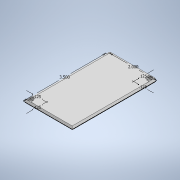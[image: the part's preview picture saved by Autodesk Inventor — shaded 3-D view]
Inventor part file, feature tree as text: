
AUTODESK INVENTOR PART (.ipt)
format: ipt  version: 2020 (Build 240168000, 168)  size: 122,880 bytes
history: native  units: in
note: dims shown in document units (in); Inventor stores cm internally (conversion verified against a paired STEP export)
features: sketch x2, extrude x1, hole x1, fillet x1
ambient origin geometry x8: Origin, YZ Plane, XZ Plane, XY Plane, X Axis, Y Axis, Z Axis, Center Point
bodies: Solid1 (feature_tree)
feature tree (5):
  sketch  "Sketch1"  dims[d0=2.0in d1=3.5in]
  extrude  "Extrusion1"  Depth=2.0in
  hole  "Hole2"  [1 undecoded]
  fillet  "Fillet1"  Radius=0.125in
  sketch  "Sketch2"  dims[d2=0.125in d3=0.125in d4=0.125in d5=0.125in d6=0.125in d7=0.0in d15=0.125in d16=0.125in d17=0.125in d18=0.125in d19=0.129in d20=0.75in d21=0.219in d22=0.0625in d23=0.5635in d24=0.25in d25=0.0in d26=0.125in]
note: 1 required parameter value undecoded (feature->parameter linkage not recoverable at this tier; creation-order binding heuristic only, values carry confidence <= 0.55)
